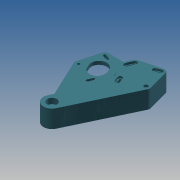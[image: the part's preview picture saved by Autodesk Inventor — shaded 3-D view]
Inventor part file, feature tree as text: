
AUTODESK INVENTOR PART (.ipt)
format: ipt  version: 2013 (Build 170138000, 138)  size: 344,576 bytes
history: native  units: mm
features: extrude x11, sketch x10, fillet x2, mirror x1, projected_geometry x1
ambient origin geometry x8: Origin, YZ Plane, XZ Plane, XY Plane, X Axis, Y Axis, Z Axis, Center Point
bodies: Solid1 (feature_tree)
feature tree (25):
  extrude  "Extrusion1"  Depth=42.0mm
  fillet  "Fillet1"  Radius=31.0mm
  extrude  "Extrusion2"  Depth=5.5mm
  extrude  "Extrusion3"  Depth=3.5mm
  mirror  "Mirror1"
  sketch  "Sketch4"  dims[d8=5.5mm d9=5.5mm]
  extrude  "Extrusion4"  Depth=5.5mm
  extrude  "Extrusion5"  Depth=5.5mm
  extrude  "Extrusion6"  Depth=5.0mm TaperAngle=0.0deg
  extrude  "Extrusion7"  Depth=5.0mm TaperAngle=0.0deg
  extrude  "Extrusion8"  Depth=8.5mm
  extrude  "Extrusion9"  Depth=22.5mm
  extrude  "Extrusion10"  Depth=20.0mm TaperAngle=0.0deg
  extrude  "Extrusion11"  Depth=6.0mm
  fillet  "Fillet4"  Radius=3.0mm
  sketch  "Sketch1"  dims[d0=198.0mm d2=42.0mm d3=31.0mm]
  sketch  "Sketch2"  dims[d4=5.5mm d5=5.5mm]
  sketch  "Sketch3"  dims[d6=5.0mm d7=3.5mm]
  projected_geometry  "Projected Loop1"
  sketch  "Sketch5"  dims[d10=5.0mm d11=0.0mm d12=5.5mm]
  sketch  "Sketch6"  dims[d13=5.0mm d14=0.0mm d15=5.0mm d16=0.0mm]
  sketch  "Sketch7"  dims[d17=25.0mm d19=5.0mm d20=0.0mm]
  sketch  "Sketch8"  dims[d21=21.0mm d22=0.0mm d23=8.5mm]
  sketch  "Sketch9"  dims[d26=20.0mm d27=0.0mm d28=22.5mm]
  sketch  "Sketch20"  dims[d30=20.0mm d31=0.0mm d32=20.0mm d33=0.0mm d34=6.0mm d36=3.0mm d37=0.0mm d38=14.0mm d40=8.0mm d41=0.0mm d57=25.0mm d58=5.5mm d59=10.0mm d60=0.0mm d61=5.5mm]
